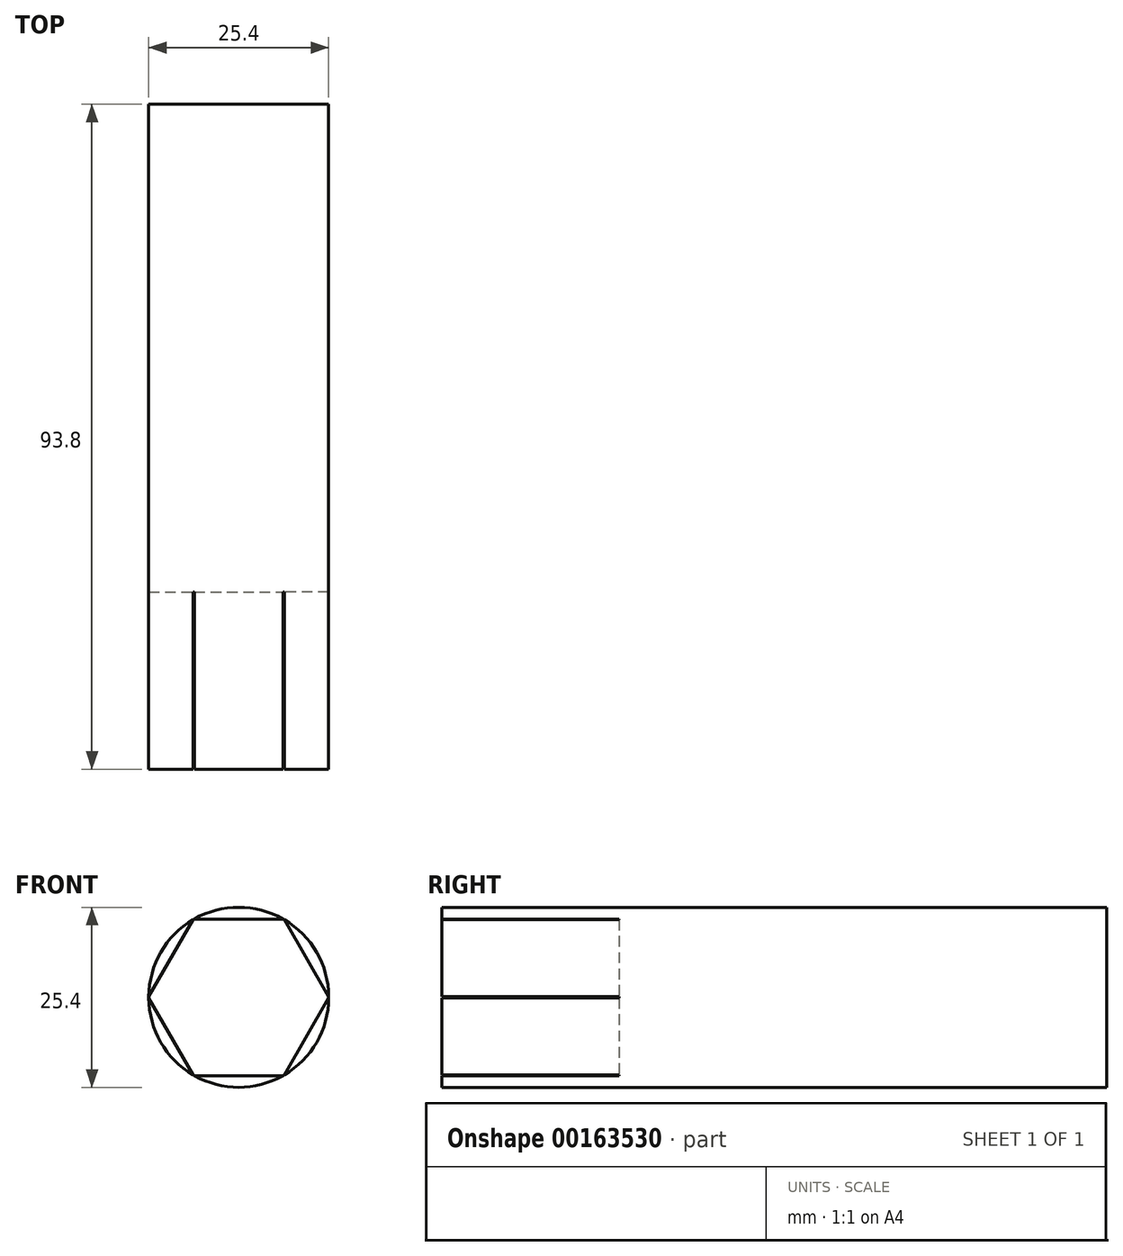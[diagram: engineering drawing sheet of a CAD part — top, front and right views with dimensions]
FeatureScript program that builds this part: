
annotation { "Feature Type Name" : "Feature", "Feature Type Description" : "" }
export const myFeature = defineFeature(function(context is Context, id is Id, definition is map)
    precondition{}
    {
        {
            var Q0;
            Q0=qCreatedBy(makeId("Front.planeOp"),FACE);
            var sketch = newSketch(context, id + "F0", { "sketchPlane" : qUnion([Q0])});
            skCircle(sketch, "E0", {"center": v(0, 0) * mm, "radius": 12.7 * mm});
            skSolve(sketch);
        }
        {
            var Q0;
            Q0=makeQuery(id+"F0.imprint","IMPRINT",FACE,{"disambiguationData":[TD([[makeQuery(id+"F0.imprint","IMPRINT",EDGE,{"derivedFrom":sQuery(id+"F0.wireOp",EDGE,"E0")}),1.0]])]});
            var Q1;
            Q1 = qSketchRegion(id + "F0", true);
            extrude(context, id + "F1", {"entities" : qUnion([Q0, Q1]), "depth" : 93.8 * mm});
        }
        {
            var Q0;
            Q0=makeQuery(id+"F1.opExtrude","CAP_FACE",FACE,{"disambiguationData":[OSD([sQuery(id+"F0.wireOp",EDGE,"E0")])],"isStart":false});
            var sketch = newSketch(context, id + "F2", { "sketchPlane" : qUnion([Q0])});
            skCircle(sketch, "E1.cCircle", {"center": v(0, 0) * mm, "radius": 11.05 * mm, "construction": true});
            skLineSegment(sketch, "E1.0", {"start": v(12.76, 0) * mm, "end": v(6.38, -11.05) * mm});
            skLineSegment(sketch, "E1.1", {"start": v(6.38, -11.05) * mm, "end": v(-6.38, -11.05) * mm});
            skLineSegment(sketch, "E1.2", {"start": v(-6.38, -11.05) * mm, "end": v(-12.76, 0) * mm});
            skLineSegment(sketch, "E1.3", {"start": v(-12.76, 0) * mm, "end": v(-6.38, 11.05) * mm});
            skLineSegment(sketch, "E1.4", {"start": v(-6.38, 11.05) * mm, "end": v(6.38, 11.05) * mm});
            skLineSegment(sketch, "E1.5", {"start": v(6.38, 11.05) * mm, "end": v(12.76, 0) * mm});
            skPoint(sketch, "E1.0.midPoint", {"position": v(9.57, -5.53) * mm});
            skSolve(sketch);
        }
        {
            var Q0;
            Q0 = qSketchRegion(id + "F2", true);
            extrude(context, id + "F3", {"entities" : qUnion([Q0]), "operationType" : NewBodyOperationType.REMOVE, "oppositeDirection" : true, "depth" : 25 * mm});
        }
    });
